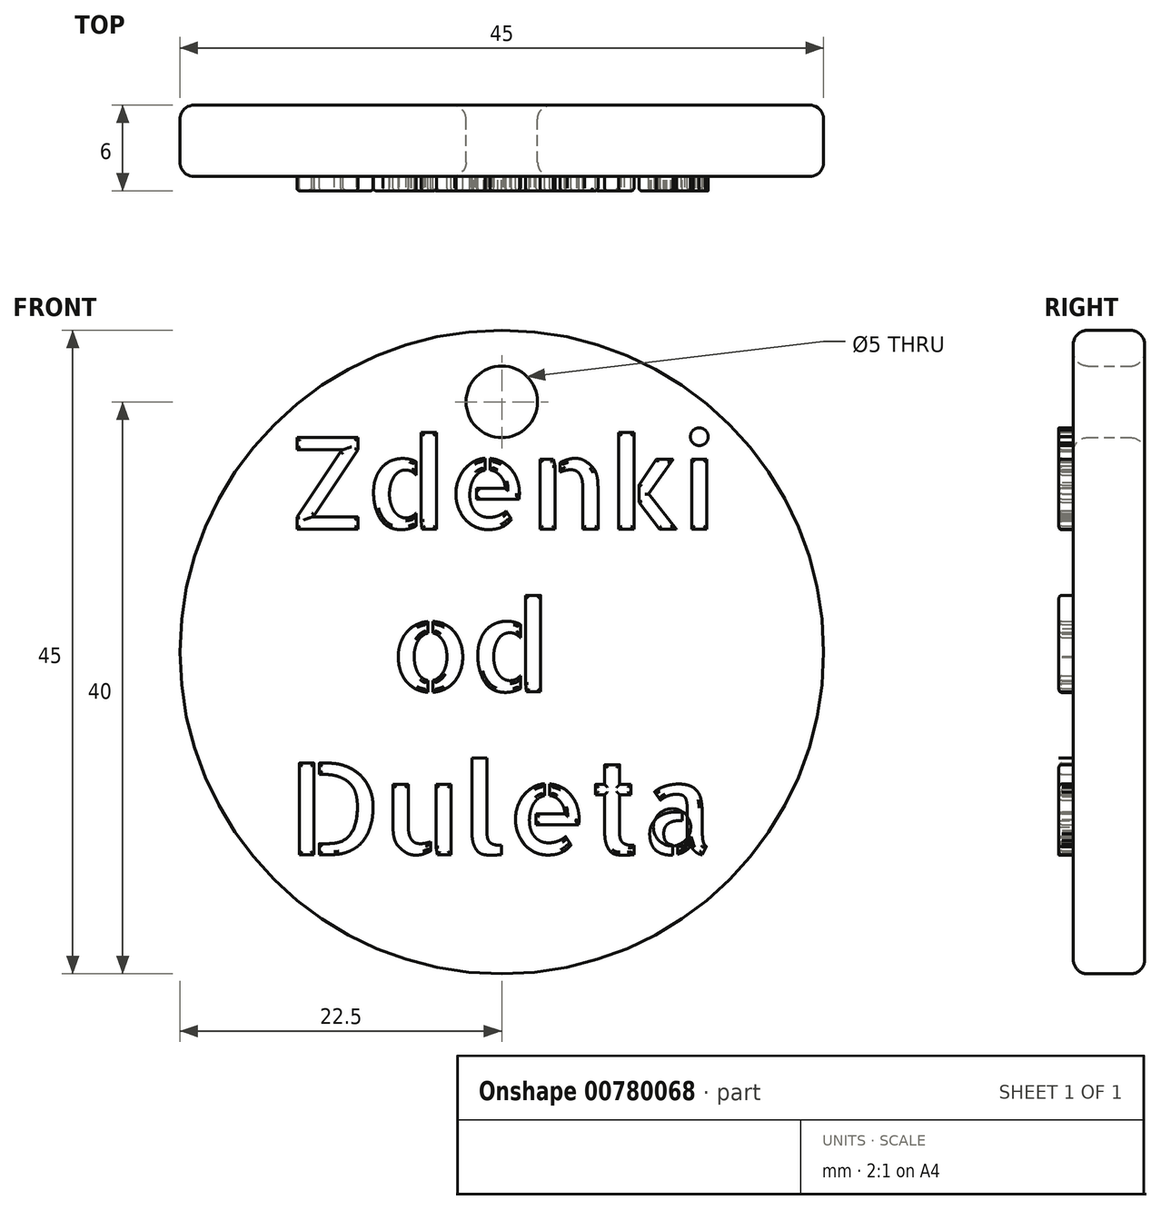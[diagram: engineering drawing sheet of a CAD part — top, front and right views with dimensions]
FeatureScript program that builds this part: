
annotation { "Feature Type Name" : "Feature", "Feature Type Description" : "" }
export const myFeature = defineFeature(function(context is Context, id is Id, definition is map)
    precondition{}
    {
        {
            var Q0;
            Q0=qCreatedBy(makeId("Front.planeOp"),FACE);
            var sketch = newSketch(context, id + "F0", { "sketchPlane" : qUnion([Q0])});
            skText(sketch, "E0", { "text": "Zdenki\n   od\nDuleta", "fontName": "AllertaStencil-Regular.ttf"});
            skCircle(sketch, "E1", {"center": v(0, 0) * mm, "radius": 22.5 * mm});
            skCircle(sketch, "E2", {"center": v(0, 17.5) * mm, "radius": 2.5 * mm});
            const initialGuessF0  = {"E0": [-0.015, 0.0086, 1, 0, 0.0064]};
            skSetInitialGuess(sketch, initialGuessF0);
            skSolve(sketch);
        }
        {
            var Q0;
            Q0=makeQuery(id+"F0.imprint","IMPRINT",FACE,{"disambiguationData":[TD([[makeQuery(id+"F0.imprint","IMPRINT",EDGE,{"derivedFrom":sQuery(id+"F0.wireOp",EDGE,"E0.sketch_text.stroke-0")}),1.0]])]});
            extrude(context, id + "F1", {"entities" : qUnion([Q0]), "depth" : 5 * mm, "offsetDistance" : 25 * mm});
        }
        {
            var Q0;
            Q0=makeQuery(id+"F0.imprint","IMPRINT",FACE,{"disambiguationData":[TD([[makeQuery(id+"F0.imprint","IMPRINT",EDGE,{"derivedFrom":sQuery(id+"F0.wireOp",EDGE,"E0.sketch_text.stroke-0")}),-1.0]])]});
            var Q1;
            Q1=makeQuery(id+"F0.imprint","IMPRINT",FACE,{"disambiguationData":[TD([[makeQuery(id+"F0.imprint","IMPRINT",EDGE,{"derivedFrom":sQuery(id+"F0.wireOp",EDGE,"E0.sketch_text.stroke-17")}),-1.0]])]});
            var Q2;
            Q2=makeQuery(id+"F0.imprint","IMPRINT",FACE,{"disambiguationData":[TD([[makeQuery(id+"F0.imprint","IMPRINT",EDGE,{"derivedFrom":sQuery(id+"F0.wireOp",EDGE,"E0.sketch_text.stroke-12")}),-1.0]])]});
            var Q3;
            Q3=makeQuery(id+"F0.imprint","IMPRINT",FACE,{"disambiguationData":[TD([[makeQuery(id+"F0.imprint","IMPRINT",EDGE,{"derivedFrom":sQuery(id+"F0.wireOp",EDGE,"E0.sketch_text.stroke-55")}),-1.0]])]});
            var Q4;
            Q4=makeQuery(id+"F0.imprint","IMPRINT",FACE,{"disambiguationData":[TD([[makeQuery(id+"F0.imprint","IMPRINT",EDGE,{"derivedFrom":sQuery(id+"F0.wireOp",EDGE,"E0.sketch_text.stroke-42")}),-1.0]])]});
            var Q5;
            Q5=makeQuery(id+"F0.imprint","IMPRINT",FACE,{"disambiguationData":[TD([[makeQuery(id+"F0.imprint","IMPRINT",EDGE,{"derivedFrom":sQuery(id+"F0.wireOp",EDGE,"E0.sketch_text.stroke-79")}),-1.0]])]});
            var Q6;
            Q6=makeQuery(id+"F0.imprint","IMPRINT",FACE,{"disambiguationData":[TD([[makeQuery(id+"F0.imprint","IMPRINT",EDGE,{"derivedFrom":sQuery(id+"F0.wireOp",EDGE,"E0.sketch_text.stroke-84")}),-1.0]])]});
            var Q7;
            Q7=makeQuery(id+"F0.imprint","IMPRINT",FACE,{"disambiguationData":[TD([[makeQuery(id+"F0.imprint","IMPRINT",EDGE,{"derivedFrom":sQuery(id+"F0.wireOp",EDGE,"E0.sketch_text.stroke-110")}),-1.0]])]});
            var Q8;
            Q8=makeQuery(id+"F0.imprint","IMPRINT",FACE,{"disambiguationData":[TD([[makeQuery(id+"F0.imprint","IMPRINT",EDGE,{"derivedFrom":sQuery(id+"F0.wireOp",EDGE,"E0.sketch_text.stroke-103")}),-1.0]])]});
            var Q9;
            Q9=makeQuery(id+"F0.imprint","IMPRINT",FACE,{"disambiguationData":[TD([[makeQuery(id+"F0.imprint","IMPRINT",EDGE,{"derivedFrom":sQuery(id+"F0.wireOp",EDGE,"E0.sketch_text.stroke-114")}),-1.0]])]});
            var Q10;
            Q10=makeQuery(id+"F0.imprint","IMPRINT",FACE,{"disambiguationData":[TD([[makeQuery(id+"F0.imprint","IMPRINT",EDGE,{"derivedFrom":sQuery(id+"F0.wireOp",EDGE,"E0.sketch_text.stroke-118")}),-1.0]])]});
            var Q11;
            Q11=makeQuery(id+"F0.imprint","IMPRINT",FACE,{"disambiguationData":[TD([[makeQuery(id+"F0.imprint","IMPRINT",EDGE,{"derivedFrom":sQuery(id+"F0.wireOp",EDGE,"E0.sketch_text.stroke-142")}),-1.0]])]});
            var Q12;
            Q12=makeQuery(id+"F0.imprint","IMPRINT",FACE,{"disambiguationData":[TD([[makeQuery(id+"F0.imprint","IMPRINT",EDGE,{"derivedFrom":sQuery(id+"F0.wireOp",EDGE,"E0.sketch_text.stroke-126")}),-1.0]])]});
            var Q13;
            Q13=makeQuery(id+"F0.imprint","IMPRINT",FACE,{"disambiguationData":[TD([[makeQuery(id+"F0.imprint","IMPRINT",EDGE,{"derivedFrom":sQuery(id+"F0.wireOp",EDGE,"E0.sketch_text.stroke-163")}),-1.0]])]});
            var Q14;
            Q14=makeQuery(id+"F0.imprint","IMPRINT",FACE,{"disambiguationData":[TD([[makeQuery(id+"F0.imprint","IMPRINT",EDGE,{"derivedFrom":sQuery(id+"F0.wireOp",EDGE,"E0.sketch_text.stroke-158")}),-1.0]])]});
            var Q15;
            Q15=makeQuery(id+"F0.imprint","IMPRINT",FACE,{"disambiguationData":[TD([[makeQuery(id+"F0.imprint","IMPRINT",EDGE,{"derivedFrom":sQuery(id+"F0.wireOp",EDGE,"E0.sketch_text.stroke-188")}),-1.0]])]});
            var Q16;
            Q16=makeQuery(id+"F0.imprint","IMPRINT",FACE,{"disambiguationData":[TD([[makeQuery(id+"F0.imprint","IMPRINT",EDGE,{"derivedFrom":sQuery(id+"F0.wireOp",EDGE,"E0.sketch_text.stroke-192")}),-1.0]])]});
            var Q17;
            Q17=makeQuery(id+"F0.imprint","IMPRINT",FACE,{"disambiguationData":[TD([[makeQuery(id+"F0.imprint","IMPRINT",EDGE,{"derivedFrom":sQuery(id+"F0.wireOp",EDGE,"E0.sketch_text.stroke-214")}),-1.0]])]});
            var Q18;
            Q18=makeQuery(id+"F0.imprint","IMPRINT",FACE,{"disambiguationData":[TD([[makeQuery(id+"F0.imprint","IMPRINT",EDGE,{"derivedFrom":sQuery(id+"F0.wireOp",EDGE,"E0.sketch_text.stroke-234")}),-1.0]])]});
            var Q19;
            Q19=makeQuery(id+"F0.imprint","IMPRINT",FACE,{"disambiguationData":[TD([[makeQuery(id+"F0.imprint","IMPRINT",EDGE,{"derivedFrom":sQuery(id+"F0.wireOp",EDGE,"E0.sketch_text.stroke-239")}),-1.0]])]});
            var Q20;
            Q20=makeQuery(id+"F0.imprint","IMPRINT",FACE,{"disambiguationData":[TD([[makeQuery(id+"F0.imprint","IMPRINT",EDGE,{"derivedFrom":sQuery(id+"F0.wireOp",EDGE,"E0.sketch_text.stroke-270")}),-1.0]])]});
            var Q21;
            Q21=makeQuery(id+"F0.imprint","IMPRINT",FACE,{"disambiguationData":[TD([[makeQuery(id+"F0.imprint","IMPRINT",EDGE,{"derivedFrom":sQuery(id+"F0.wireOp",EDGE,"E0.sketch_text.stroke-257")}),-1.0]])]});
            var Q22;
            Q22=makeQuery(id+"F0.imprint","IMPRINT",FACE,{"disambiguationData":[TD([[makeQuery(id+"F0.imprint","IMPRINT",EDGE,{"derivedFrom":sQuery(id+"F0.wireOp",EDGE,"E0.sketch_text.stroke-294")}),-1.0]])]});
            var Q23;
            Q23=makeQuery(id+"F0.imprint","IMPRINT",FACE,{"disambiguationData":[TD([[makeQuery(id+"F0.imprint","IMPRINT",EDGE,{"derivedFrom":sQuery(id+"F0.wireOp",EDGE,"E0.sketch_text.stroke-319")}),-1.0]])]});
            var Q24;
            Q24=makeQuery(id+"F0.imprint","IMPRINT",FACE,{"disambiguationData":[TD([[makeQuery(id+"F0.imprint","IMPRINT",EDGE,{"derivedFrom":sQuery(id+"F0.wireOp",EDGE,"E0.sketch_text.stroke-338")}),-1.0]])]});
            extrude(context, id + "F2", {"entities" : qUnion([Q0, Q1, Q2, Q3, Q4, Q5, Q6, Q7, Q8, Q9, Q10, Q11, Q12, Q13, Q14, Q15, Q16, Q17, Q18, Q19, Q20, Q21, Q22, Q23, Q24]), "operationType" : NewBodyOperationType.ADD, "depth" : 6 * mm, "offsetDistance" : 25 * mm});
        }
        {
            var Q0;
            Q0=makeQuery(id+"F0.imprint","IMPRINT",FACE,{"disambiguationData":[TD([[makeQuery(id+"F0.imprint","IMPRINT",EDGE,{"derivedFrom":sQuery(id+"F0.wireOp",EDGE,"E2")}),1.0]])]});
            extrude(context, id + "F3", {"entities" : qUnion([Q0]), "operationType" : NewBodyOperationType.REMOVE, "endBound" : BoundingType.THROUGH_ALL, "depth" : 25 * mm, "offsetDistance" : 25 * mm});
        }
        {
            var Q0;
            Q0=makeQuery(id+"F1.opExtrude","SWEPT_FACE",FACE,{"disambiguationData":[OSD([sQuery(id+"F0.wireOp",EDGE,"E2")])]});
            var Q1;
            Q1=makeQuery(id+"F1.opExtrude","SWEPT_FACE",FACE,{"disambiguationData":[OSD([sQuery(id+"F0.wireOp",EDGE,"E1")])]});
            fillet(context, id + "F4", {"entities" : qUnion([Q0, Q1]), "radius" : 1 * mm, "tangentPropagation" : true, "allowEdgeOverflow" : false});
        }
        {
            var Q0;
            Q0=makeQuery(id+"F2.opExtrude","CAP_FACE",FACE,{"disambiguationData":[OSD([sQuery(id+"F0.wireOp",EDGE,"E0.sketch_text.stroke-0"),sQuery(id+"F0.wireOp",EDGE,"E0.sketch_text.stroke-1"),sQuery(id+"F0.wireOp",EDGE,"E0.sketch_text.stroke-2"),sQuery(id+"F0.wireOp",EDGE,"E0.sketch_text.stroke-3"),sQuery(id+"F0.wireOp",EDGE,"E0.sketch_text.stroke-4"),sQuery(id+"F0.wireOp",EDGE,"E0.sketch_text.stroke-5"),sQuery(id+"F0.wireOp",EDGE,"E0.sketch_text.stroke-6"),sQuery(id+"F0.wireOp",EDGE,"E0.sketch_text.stroke-7"),sQuery(id+"F0.wireOp",EDGE,"E0.sketch_text.stroke-8"),sQuery(id+"F0.wireOp",EDGE,"E0.sketch_text.stroke-9"),sQuery(id+"F0.wireOp",EDGE,"E0.sketch_text.stroke-10"),sQuery(id+"F0.wireOp",EDGE,"E0.sketch_text.stroke-11")])],"isStart":false});
            var Q1;
            Q1=makeQuery(id+"F2.opExtrude","CAP_FACE",FACE,{"disambiguationData":[OSD([sQuery(id+"F0.wireOp",EDGE,"E0.sketch_text.stroke-17"),sQuery(id+"F0.wireOp",EDGE,"E0.sketch_text.stroke-18"),sQuery(id+"F0.wireOp",EDGE,"E0.sketch_text.stroke-19"),sQuery(id+"F0.wireOp",EDGE,"E0.sketch_text.stroke-20"),sQuery(id+"F0.wireOp",EDGE,"E0.sketch_text.stroke-21"),sQuery(id+"F0.wireOp",EDGE,"E0.sketch_text.stroke-22"),sQuery(id+"F0.wireOp",EDGE,"E0.sketch_text.stroke-23"),sQuery(id+"F0.wireOp",EDGE,"E0.sketch_text.stroke-24"),sQuery(id+"F0.wireOp",EDGE,"E0.sketch_text.stroke-25"),sQuery(id+"F0.wireOp",EDGE,"E0.sketch_text.stroke-26"),sQuery(id+"F0.wireOp",EDGE,"E0.sketch_text.stroke-27"),sQuery(id+"F0.wireOp",EDGE,"E0.sketch_text.stroke-28"),sQuery(id+"F0.wireOp",EDGE,"E0.sketch_text.stroke-29"),sQuery(id+"F0.wireOp",EDGE,"E0.sketch_text.stroke-30"),sQuery(id+"F0.wireOp",EDGE,"E0.sketch_text.stroke-31"),sQuery(id+"F0.wireOp",EDGE,"E0.sketch_text.stroke-32"),sQuery(id+"F0.wireOp",EDGE,"E0.sketch_text.stroke-33"),sQuery(id+"F0.wireOp",EDGE,"E0.sketch_text.stroke-34"),sQuery(id+"F0.wireOp",EDGE,"E0.sketch_text.stroke-35"),sQuery(id+"F0.wireOp",EDGE,"E0.sketch_text.stroke-36"),sQuery(id+"F0.wireOp",EDGE,"E0.sketch_text.stroke-37"),sQuery(id+"F0.wireOp",EDGE,"E0.sketch_text.stroke-38"),sQuery(id+"F0.wireOp",EDGE,"E0.sketch_text.stroke-39"),sQuery(id+"F0.wireOp",EDGE,"E0.sketch_text.stroke-40"),sQuery(id+"F0.wireOp",EDGE,"E0.sketch_text.stroke-41")])],"isStart":false});
            var Q2;
            Q2=makeQuery(id+"F2.opExtrude","CAP_FACE",FACE,{"disambiguationData":[OSD([sQuery(id+"F0.wireOp",EDGE,"E0.sketch_text.stroke-12"),sQuery(id+"F0.wireOp",EDGE,"E0.sketch_text.stroke-13"),sQuery(id+"F0.wireOp",EDGE,"E0.sketch_text.stroke-14"),sQuery(id+"F0.wireOp",EDGE,"E0.sketch_text.stroke-15"),sQuery(id+"F0.wireOp",EDGE,"E0.sketch_text.stroke-16")])],"isStart":false});
            var Q3;
            Q3=makeQuery(id+"F2.opExtrude","CAP_FACE",FACE,{"disambiguationData":[OSD([sQuery(id+"F0.wireOp",EDGE,"E0.sketch_text.stroke-55"),sQuery(id+"F0.wireOp",EDGE,"E0.sketch_text.stroke-56"),sQuery(id+"F0.wireOp",EDGE,"E0.sketch_text.stroke-57"),sQuery(id+"F0.wireOp",EDGE,"E0.sketch_text.stroke-58"),sQuery(id+"F0.wireOp",EDGE,"E0.sketch_text.stroke-59"),sQuery(id+"F0.wireOp",EDGE,"E0.sketch_text.stroke-60"),sQuery(id+"F0.wireOp",EDGE,"E0.sketch_text.stroke-61"),sQuery(id+"F0.wireOp",EDGE,"E0.sketch_text.stroke-62"),sQuery(id+"F0.wireOp",EDGE,"E0.sketch_text.stroke-63"),sQuery(id+"F0.wireOp",EDGE,"E0.sketch_text.stroke-64"),sQuery(id+"F0.wireOp",EDGE,"E0.sketch_text.stroke-65"),sQuery(id+"F0.wireOp",EDGE,"E0.sketch_text.stroke-66"),sQuery(id+"F0.wireOp",EDGE,"E0.sketch_text.stroke-67"),sQuery(id+"F0.wireOp",EDGE,"E0.sketch_text.stroke-68"),sQuery(id+"F0.wireOp",EDGE,"E0.sketch_text.stroke-69"),sQuery(id+"F0.wireOp",EDGE,"E0.sketch_text.stroke-70"),sQuery(id+"F0.wireOp",EDGE,"E0.sketch_text.stroke-71"),sQuery(id+"F0.wireOp",EDGE,"E0.sketch_text.stroke-72"),sQuery(id+"F0.wireOp",EDGE,"E0.sketch_text.stroke-73"),sQuery(id+"F0.wireOp",EDGE,"E0.sketch_text.stroke-74"),sQuery(id+"F0.wireOp",EDGE,"E0.sketch_text.stroke-75"),sQuery(id+"F0.wireOp",EDGE,"E0.sketch_text.stroke-76"),sQuery(id+"F0.wireOp",EDGE,"E0.sketch_text.stroke-77"),sQuery(id+"F0.wireOp",EDGE,"E0.sketch_text.stroke-78")])],"isStart":false});
            var Q4;
            Q4=makeQuery(id+"F2.opExtrude","CAP_FACE",FACE,{"disambiguationData":[OSD([sQuery(id+"F0.wireOp",EDGE,"E0.sketch_text.stroke-42"),sQuery(id+"F0.wireOp",EDGE,"E0.sketch_text.stroke-43"),sQuery(id+"F0.wireOp",EDGE,"E0.sketch_text.stroke-44"),sQuery(id+"F0.wireOp",EDGE,"E0.sketch_text.stroke-45"),sQuery(id+"F0.wireOp",EDGE,"E0.sketch_text.stroke-46"),sQuery(id+"F0.wireOp",EDGE,"E0.sketch_text.stroke-47"),sQuery(id+"F0.wireOp",EDGE,"E0.sketch_text.stroke-48"),sQuery(id+"F0.wireOp",EDGE,"E0.sketch_text.stroke-49"),sQuery(id+"F0.wireOp",EDGE,"E0.sketch_text.stroke-50"),sQuery(id+"F0.wireOp",EDGE,"E0.sketch_text.stroke-51"),sQuery(id+"F0.wireOp",EDGE,"E0.sketch_text.stroke-52"),sQuery(id+"F0.wireOp",EDGE,"E0.sketch_text.stroke-53"),sQuery(id+"F0.wireOp",EDGE,"E0.sketch_text.stroke-54")])],"isStart":false});
            var Q5;
            Q5=makeQuery(id+"F2.opExtrude","CAP_FACE",FACE,{"disambiguationData":[OSD([sQuery(id+"F0.wireOp",EDGE,"E0.sketch_text.stroke-79"),sQuery(id+"F0.wireOp",EDGE,"E0.sketch_text.stroke-80"),sQuery(id+"F0.wireOp",EDGE,"E0.sketch_text.stroke-81"),sQuery(id+"F0.wireOp",EDGE,"E0.sketch_text.stroke-82"),sQuery(id+"F0.wireOp",EDGE,"E0.sketch_text.stroke-83")])],"isStart":false});
            var Q6;
            Q6=makeQuery(id+"F2.opExtrude","CAP_FACE",FACE,{"disambiguationData":[OSD([sQuery(id+"F0.wireOp",EDGE,"E0.sketch_text.stroke-84"),sQuery(id+"F0.wireOp",EDGE,"E0.sketch_text.stroke-85"),sQuery(id+"F0.wireOp",EDGE,"E0.sketch_text.stroke-86"),sQuery(id+"F0.wireOp",EDGE,"E0.sketch_text.stroke-87"),sQuery(id+"F0.wireOp",EDGE,"E0.sketch_text.stroke-88"),sQuery(id+"F0.wireOp",EDGE,"E0.sketch_text.stroke-89"),sQuery(id+"F0.wireOp",EDGE,"E0.sketch_text.stroke-90"),sQuery(id+"F0.wireOp",EDGE,"E0.sketch_text.stroke-91"),sQuery(id+"F0.wireOp",EDGE,"E0.sketch_text.stroke-92"),sQuery(id+"F0.wireOp",EDGE,"E0.sketch_text.stroke-93"),sQuery(id+"F0.wireOp",EDGE,"E0.sketch_text.stroke-94"),sQuery(id+"F0.wireOp",EDGE,"E0.sketch_text.stroke-95"),sQuery(id+"F0.wireOp",EDGE,"E0.sketch_text.stroke-96"),sQuery(id+"F0.wireOp",EDGE,"E0.sketch_text.stroke-97"),sQuery(id+"F0.wireOp",EDGE,"E0.sketch_text.stroke-98"),sQuery(id+"F0.wireOp",EDGE,"E0.sketch_text.stroke-99"),sQuery(id+"F0.wireOp",EDGE,"E0.sketch_text.stroke-100"),sQuery(id+"F0.wireOp",EDGE,"E0.sketch_text.stroke-101"),sQuery(id+"F0.wireOp",EDGE,"E0.sketch_text.stroke-102")])],"isStart":false});
            var Q7;
            Q7=makeQuery(id+"F2.opExtrude","CAP_FACE",FACE,{"disambiguationData":[OSD([sQuery(id+"F0.wireOp",EDGE,"E0.sketch_text.stroke-110"),sQuery(id+"F0.wireOp",EDGE,"E0.sketch_text.stroke-111"),sQuery(id+"F0.wireOp",EDGE,"E0.sketch_text.stroke-112"),sQuery(id+"F0.wireOp",EDGE,"E0.sketch_text.stroke-113")])],"isStart":false});
            var Q8;
            Q8=makeQuery(id+"F2.opExtrude","CAP_FACE",FACE,{"disambiguationData":[OSD([sQuery(id+"F0.wireOp",EDGE,"E0.sketch_text.stroke-103"),sQuery(id+"F0.wireOp",EDGE,"E0.sketch_text.stroke-104"),sQuery(id+"F0.wireOp",EDGE,"E0.sketch_text.stroke-105"),sQuery(id+"F0.wireOp",EDGE,"E0.sketch_text.stroke-106"),sQuery(id+"F0.wireOp",EDGE,"E0.sketch_text.stroke-107"),sQuery(id+"F0.wireOp",EDGE,"E0.sketch_text.stroke-108"),sQuery(id+"F0.wireOp",EDGE,"E0.sketch_text.stroke-109")])],"isStart":false});
            var Q9;
            Q9=makeQuery(id+"F2.opExtrude","CAP_FACE",FACE,{"disambiguationData":[OSD([sQuery(id+"F0.wireOp",EDGE,"E0.sketch_text.stroke-114"),sQuery(id+"F0.wireOp",EDGE,"E0.sketch_text.stroke-115"),sQuery(id+"F0.wireOp",EDGE,"E0.sketch_text.stroke-116"),sQuery(id+"F0.wireOp",EDGE,"E0.sketch_text.stroke-117")])],"isStart":false});
            var Q10;
            Q10=makeQuery(id+"F2.opExtrude","CAP_FACE",FACE,{"disambiguationData":[OSD([sQuery(id+"F0.wireOp",EDGE,"E0.sketch_text.stroke-158"),sQuery(id+"F0.wireOp",EDGE,"E0.sketch_text.stroke-159"),sQuery(id+"F0.wireOp",EDGE,"E0.sketch_text.stroke-160"),sQuery(id+"F0.wireOp",EDGE,"E0.sketch_text.stroke-161"),sQuery(id+"F0.wireOp",EDGE,"E0.sketch_text.stroke-162")])],"isStart":false});
            var Q11;
            Q11=makeQuery(id+"F2.opExtrude","CAP_FACE",FACE,{"disambiguationData":[OSD([sQuery(id+"F0.wireOp",EDGE,"E0.sketch_text.stroke-163"),sQuery(id+"F0.wireOp",EDGE,"E0.sketch_text.stroke-164"),sQuery(id+"F0.wireOp",EDGE,"E0.sketch_text.stroke-165"),sQuery(id+"F0.wireOp",EDGE,"E0.sketch_text.stroke-166"),sQuery(id+"F0.wireOp",EDGE,"E0.sketch_text.stroke-167"),sQuery(id+"F0.wireOp",EDGE,"E0.sketch_text.stroke-168"),sQuery(id+"F0.wireOp",EDGE,"E0.sketch_text.stroke-169"),sQuery(id+"F0.wireOp",EDGE,"E0.sketch_text.stroke-170"),sQuery(id+"F0.wireOp",EDGE,"E0.sketch_text.stroke-171"),sQuery(id+"F0.wireOp",EDGE,"E0.sketch_text.stroke-172"),sQuery(id+"F0.wireOp",EDGE,"E0.sketch_text.stroke-173"),sQuery(id+"F0.wireOp",EDGE,"E0.sketch_text.stroke-174"),sQuery(id+"F0.wireOp",EDGE,"E0.sketch_text.stroke-175"),sQuery(id+"F0.wireOp",EDGE,"E0.sketch_text.stroke-176"),sQuery(id+"F0.wireOp",EDGE,"E0.sketch_text.stroke-177"),sQuery(id+"F0.wireOp",EDGE,"E0.sketch_text.stroke-178"),sQuery(id+"F0.wireOp",EDGE,"E0.sketch_text.stroke-179"),sQuery(id+"F0.wireOp",EDGE,"E0.sketch_text.stroke-180"),sQuery(id+"F0.wireOp",EDGE,"E0.sketch_text.stroke-181"),sQuery(id+"F0.wireOp",EDGE,"E0.sketch_text.stroke-182"),sQuery(id+"F0.wireOp",EDGE,"E0.sketch_text.stroke-183"),sQuery(id+"F0.wireOp",EDGE,"E0.sketch_text.stroke-184"),sQuery(id+"F0.wireOp",EDGE,"E0.sketch_text.stroke-185"),sQuery(id+"F0.wireOp",EDGE,"E0.sketch_text.stroke-186"),sQuery(id+"F0.wireOp",EDGE,"E0.sketch_text.stroke-187")])],"isStart":false});
            var Q12;
            Q12=makeQuery(id+"F2.opExtrude","CAP_FACE",FACE,{"disambiguationData":[OSD([sQuery(id+"F0.wireOp",EDGE,"E0.sketch_text.stroke-126"),sQuery(id+"F0.wireOp",EDGE,"E0.sketch_text.stroke-127"),sQuery(id+"F0.wireOp",EDGE,"E0.sketch_text.stroke-128"),sQuery(id+"F0.wireOp",EDGE,"E0.sketch_text.stroke-129"),sQuery(id+"F0.wireOp",EDGE,"E0.sketch_text.stroke-130"),sQuery(id+"F0.wireOp",EDGE,"E0.sketch_text.stroke-131"),sQuery(id+"F0.wireOp",EDGE,"E0.sketch_text.stroke-132"),sQuery(id+"F0.wireOp",EDGE,"E0.sketch_text.stroke-133"),sQuery(id+"F0.wireOp",EDGE,"E0.sketch_text.stroke-134"),sQuery(id+"F0.wireOp",EDGE,"E0.sketch_text.stroke-135"),sQuery(id+"F0.wireOp",EDGE,"E0.sketch_text.stroke-136"),sQuery(id+"F0.wireOp",EDGE,"E0.sketch_text.stroke-137"),sQuery(id+"F0.wireOp",EDGE,"E0.sketch_text.stroke-138"),sQuery(id+"F0.wireOp",EDGE,"E0.sketch_text.stroke-139"),sQuery(id+"F0.wireOp",EDGE,"E0.sketch_text.stroke-140"),sQuery(id+"F0.wireOp",EDGE,"E0.sketch_text.stroke-141")])],"isStart":false});
            var Q13;
            Q13=makeQuery(id+"F2.opExtrude","CAP_FACE",FACE,{"disambiguationData":[OSD([sQuery(id+"F0.wireOp",EDGE,"E0.sketch_text.stroke-142"),sQuery(id+"F0.wireOp",EDGE,"E0.sketch_text.stroke-143"),sQuery(id+"F0.wireOp",EDGE,"E0.sketch_text.stroke-144"),sQuery(id+"F0.wireOp",EDGE,"E0.sketch_text.stroke-145"),sQuery(id+"F0.wireOp",EDGE,"E0.sketch_text.stroke-146"),sQuery(id+"F0.wireOp",EDGE,"E0.sketch_text.stroke-147"),sQuery(id+"F0.wireOp",EDGE,"E0.sketch_text.stroke-148"),sQuery(id+"F0.wireOp",EDGE,"E0.sketch_text.stroke-149"),sQuery(id+"F0.wireOp",EDGE,"E0.sketch_text.stroke-150"),sQuery(id+"F0.wireOp",EDGE,"E0.sketch_text.stroke-151"),sQuery(id+"F0.wireOp",EDGE,"E0.sketch_text.stroke-152"),sQuery(id+"F0.wireOp",EDGE,"E0.sketch_text.stroke-153"),sQuery(id+"F0.wireOp",EDGE,"E0.sketch_text.stroke-154"),sQuery(id+"F0.wireOp",EDGE,"E0.sketch_text.stroke-155"),sQuery(id+"F0.wireOp",EDGE,"E0.sketch_text.stroke-156"),sQuery(id+"F0.wireOp",EDGE,"E0.sketch_text.stroke-157")])],"isStart":false});
            var Q14;
            Q14=makeQuery(id+"F2.opExtrude","CAP_FACE",FACE,{"disambiguationData":[OSD([sQuery(id+"F0.wireOp",EDGE,"E0.sketch_text.stroke-188"),sQuery(id+"F0.wireOp",EDGE,"E0.sketch_text.stroke-189"),sQuery(id+"F0.wireOp",EDGE,"E0.sketch_text.stroke-190"),sQuery(id+"F0.wireOp",EDGE,"E0.sketch_text.stroke-191")])],"isStart":false});
            var Q15;
            Q15=makeQuery(id+"F2.opExtrude","CAP_FACE",FACE,{"disambiguationData":[OSD([sQuery(id+"F0.wireOp",EDGE,"E0.sketch_text.stroke-192"),sQuery(id+"F0.wireOp",EDGE,"E0.sketch_text.stroke-193"),sQuery(id+"F0.wireOp",EDGE,"E0.sketch_text.stroke-194"),sQuery(id+"F0.wireOp",EDGE,"E0.sketch_text.stroke-195"),sQuery(id+"F0.wireOp",EDGE,"E0.sketch_text.stroke-196"),sQuery(id+"F0.wireOp",EDGE,"E0.sketch_text.stroke-197"),sQuery(id+"F0.wireOp",EDGE,"E0.sketch_text.stroke-198"),sQuery(id+"F0.wireOp",EDGE,"E0.sketch_text.stroke-199"),sQuery(id+"F0.wireOp",EDGE,"E0.sketch_text.stroke-200"),sQuery(id+"F0.wireOp",EDGE,"E0.sketch_text.stroke-201"),sQuery(id+"F0.wireOp",EDGE,"E0.sketch_text.stroke-202"),sQuery(id+"F0.wireOp",EDGE,"E0.sketch_text.stroke-203"),sQuery(id+"F0.wireOp",EDGE,"E0.sketch_text.stroke-204"),sQuery(id+"F0.wireOp",EDGE,"E0.sketch_text.stroke-205"),sQuery(id+"F0.wireOp",EDGE,"E0.sketch_text.stroke-206"),sQuery(id+"F0.wireOp",EDGE,"E0.sketch_text.stroke-207"),sQuery(id+"F0.wireOp",EDGE,"E0.sketch_text.stroke-208"),sQuery(id+"F0.wireOp",EDGE,"E0.sketch_text.stroke-209"),sQuery(id+"F0.wireOp",EDGE,"E0.sketch_text.stroke-210"),sQuery(id+"F0.wireOp",EDGE,"E0.sketch_text.stroke-211"),sQuery(id+"F0.wireOp",EDGE,"E0.sketch_text.stroke-212"),sQuery(id+"F0.wireOp",EDGE,"E0.sketch_text.stroke-213")])],"isStart":false});
            var Q16;
            Q16=makeQuery(id+"F2.opExtrude","CAP_FACE",FACE,{"disambiguationData":[OSD([sQuery(id+"F0.wireOp",EDGE,"E0.sketch_text.stroke-214"),sQuery(id+"F0.wireOp",EDGE,"E0.sketch_text.stroke-215"),sQuery(id+"F0.wireOp",EDGE,"E0.sketch_text.stroke-216"),sQuery(id+"F0.wireOp",EDGE,"E0.sketch_text.stroke-217"),sQuery(id+"F0.wireOp",EDGE,"E0.sketch_text.stroke-218"),sQuery(id+"F0.wireOp",EDGE,"E0.sketch_text.stroke-219"),sQuery(id+"F0.wireOp",EDGE,"E0.sketch_text.stroke-220"),sQuery(id+"F0.wireOp",EDGE,"E0.sketch_text.stroke-221"),sQuery(id+"F0.wireOp",EDGE,"E0.sketch_text.stroke-222"),sQuery(id+"F0.wireOp",EDGE,"E0.sketch_text.stroke-223"),sQuery(id+"F0.wireOp",EDGE,"E0.sketch_text.stroke-224"),sQuery(id+"F0.wireOp",EDGE,"E0.sketch_text.stroke-225"),sQuery(id+"F0.wireOp",EDGE,"E0.sketch_text.stroke-226"),sQuery(id+"F0.wireOp",EDGE,"E0.sketch_text.stroke-227"),sQuery(id+"F0.wireOp",EDGE,"E0.sketch_text.stroke-228"),sQuery(id+"F0.wireOp",EDGE,"E0.sketch_text.stroke-229"),sQuery(id+"F0.wireOp",EDGE,"E0.sketch_text.stroke-230"),sQuery(id+"F0.wireOp",EDGE,"E0.sketch_text.stroke-231"),sQuery(id+"F0.wireOp",EDGE,"E0.sketch_text.stroke-232"),sQuery(id+"F0.wireOp",EDGE,"E0.sketch_text.stroke-233")])],"isStart":false});
            var Q17;
            Q17=makeQuery(id+"F2.opExtrude","CAP_FACE",FACE,{"disambiguationData":[OSD([sQuery(id+"F0.wireOp",EDGE,"E0.sketch_text.stroke-234"),sQuery(id+"F0.wireOp",EDGE,"E0.sketch_text.stroke-235"),sQuery(id+"F0.wireOp",EDGE,"E0.sketch_text.stroke-236"),sQuery(id+"F0.wireOp",EDGE,"E0.sketch_text.stroke-237"),sQuery(id+"F0.wireOp",EDGE,"E0.sketch_text.stroke-238")])],"isStart":false});
            var Q18;
            Q18=makeQuery(id+"F2.opExtrude","CAP_FACE",FACE,{"disambiguationData":[OSD([sQuery(id+"F0.wireOp",EDGE,"E0.sketch_text.stroke-270"),sQuery(id+"F0.wireOp",EDGE,"E0.sketch_text.stroke-271"),sQuery(id+"F0.wireOp",EDGE,"E0.sketch_text.stroke-272"),sQuery(id+"F0.wireOp",EDGE,"E0.sketch_text.stroke-273"),sQuery(id+"F0.wireOp",EDGE,"E0.sketch_text.stroke-274"),sQuery(id+"F0.wireOp",EDGE,"E0.sketch_text.stroke-275"),sQuery(id+"F0.wireOp",EDGE,"E0.sketch_text.stroke-276"),sQuery(id+"F0.wireOp",EDGE,"E0.sketch_text.stroke-277"),sQuery(id+"F0.wireOp",EDGE,"E0.sketch_text.stroke-278"),sQuery(id+"F0.wireOp",EDGE,"E0.sketch_text.stroke-279"),sQuery(id+"F0.wireOp",EDGE,"E0.sketch_text.stroke-280"),sQuery(id+"F0.wireOp",EDGE,"E0.sketch_text.stroke-281"),sQuery(id+"F0.wireOp",EDGE,"E0.sketch_text.stroke-282"),sQuery(id+"F0.wireOp",EDGE,"E0.sketch_text.stroke-283"),sQuery(id+"F0.wireOp",EDGE,"E0.sketch_text.stroke-284"),sQuery(id+"F0.wireOp",EDGE,"E0.sketch_text.stroke-285"),sQuery(id+"F0.wireOp",EDGE,"E0.sketch_text.stroke-286"),sQuery(id+"F0.wireOp",EDGE,"E0.sketch_text.stroke-287"),sQuery(id+"F0.wireOp",EDGE,"E0.sketch_text.stroke-288"),sQuery(id+"F0.wireOp",EDGE,"E0.sketch_text.stroke-289"),sQuery(id+"F0.wireOp",EDGE,"E0.sketch_text.stroke-290"),sQuery(id+"F0.wireOp",EDGE,"E0.sketch_text.stroke-291"),sQuery(id+"F0.wireOp",EDGE,"E0.sketch_text.stroke-292"),sQuery(id+"F0.wireOp",EDGE,"E0.sketch_text.stroke-293")])],"isStart":false});
            var Q19;
            Q19=makeQuery(id+"F2.opExtrude","CAP_FACE",FACE,{"disambiguationData":[OSD([sQuery(id+"F0.wireOp",EDGE,"E0.sketch_text.stroke-257"),sQuery(id+"F0.wireOp",EDGE,"E0.sketch_text.stroke-258"),sQuery(id+"F0.wireOp",EDGE,"E0.sketch_text.stroke-259"),sQuery(id+"F0.wireOp",EDGE,"E0.sketch_text.stroke-260"),sQuery(id+"F0.wireOp",EDGE,"E0.sketch_text.stroke-261"),sQuery(id+"F0.wireOp",EDGE,"E0.sketch_text.stroke-262"),sQuery(id+"F0.wireOp",EDGE,"E0.sketch_text.stroke-263"),sQuery(id+"F0.wireOp",EDGE,"E0.sketch_text.stroke-264"),sQuery(id+"F0.wireOp",EDGE,"E0.sketch_text.stroke-265"),sQuery(id+"F0.wireOp",EDGE,"E0.sketch_text.stroke-266"),sQuery(id+"F0.wireOp",EDGE,"E0.sketch_text.stroke-267"),sQuery(id+"F0.wireOp",EDGE,"E0.sketch_text.stroke-268"),sQuery(id+"F0.wireOp",EDGE,"E0.sketch_text.stroke-269")])],"isStart":false});
            var Q20;
            Q20=makeQuery(id+"F2.opExtrude","CAP_FACE",FACE,{"disambiguationData":[OSD([sQuery(id+"F0.wireOp",EDGE,"E0.sketch_text.stroke-294"),sQuery(id+"F0.wireOp",EDGE,"E0.sketch_text.stroke-295"),sQuery(id+"F0.wireOp",EDGE,"E0.sketch_text.stroke-296"),sQuery(id+"F0.wireOp",EDGE,"E0.sketch_text.stroke-297"),sQuery(id+"F0.wireOp",EDGE,"E0.sketch_text.stroke-298"),sQuery(id+"F0.wireOp",EDGE,"E0.sketch_text.stroke-299"),sQuery(id+"F0.wireOp",EDGE,"E0.sketch_text.stroke-300"),sQuery(id+"F0.wireOp",EDGE,"E0.sketch_text.stroke-301"),sQuery(id+"F0.wireOp",EDGE,"E0.sketch_text.stroke-302"),sQuery(id+"F0.wireOp",EDGE,"E0.sketch_text.stroke-303"),sQuery(id+"F0.wireOp",EDGE,"E0.sketch_text.stroke-304"),sQuery(id+"F0.wireOp",EDGE,"E0.sketch_text.stroke-305"),sQuery(id+"F0.wireOp",EDGE,"E0.sketch_text.stroke-306"),sQuery(id+"F0.wireOp",EDGE,"E0.sketch_text.stroke-307"),sQuery(id+"F0.wireOp",EDGE,"E0.sketch_text.stroke-308"),sQuery(id+"F0.wireOp",EDGE,"E0.sketch_text.stroke-309"),sQuery(id+"F0.wireOp",EDGE,"E0.sketch_text.stroke-310"),sQuery(id+"F0.wireOp",EDGE,"E0.sketch_text.stroke-311"),sQuery(id+"F0.wireOp",EDGE,"E0.sketch_text.stroke-312"),sQuery(id+"F0.wireOp",EDGE,"E0.sketch_text.stroke-313"),sQuery(id+"F0.wireOp",EDGE,"E0.sketch_text.stroke-314"),sQuery(id+"F0.wireOp",EDGE,"E0.sketch_text.stroke-315"),sQuery(id+"F0.wireOp",EDGE,"E0.sketch_text.stroke-316"),sQuery(id+"F0.wireOp",EDGE,"E0.sketch_text.stroke-317"),sQuery(id+"F0.wireOp",EDGE,"E0.sketch_text.stroke-318")])],"isStart":false});
            var Q21;
            Q21=makeQuery(id+"F2.opExtrude","CAP_FACE",FACE,{"disambiguationData":[OSD([sQuery(id+"F0.wireOp",EDGE,"E0.sketch_text.stroke-338"),sQuery(id+"F0.wireOp",EDGE,"E0.sketch_text.stroke-339"),sQuery(id+"F0.wireOp",EDGE,"E0.sketch_text.stroke-340"),sQuery(id+"F0.wireOp",EDGE,"E0.sketch_text.stroke-341"),sQuery(id+"F0.wireOp",EDGE,"E0.sketch_text.stroke-342"),sQuery(id+"F0.wireOp",EDGE,"E0.sketch_text.stroke-343"),sQuery(id+"F0.wireOp",EDGE,"E0.sketch_text.stroke-344"),sQuery(id+"F0.wireOp",EDGE,"E0.sketch_text.stroke-345"),sQuery(id+"F0.wireOp",EDGE,"E0.sketch_text.stroke-346"),sQuery(id+"F0.wireOp",EDGE,"E0.sketch_text.stroke-347"),sQuery(id+"F0.wireOp",EDGE,"E0.sketch_text.stroke-348"),sQuery(id+"F0.wireOp",EDGE,"E0.sketch_text.stroke-349"),sQuery(id+"F0.wireOp",EDGE,"E0.sketch_text.stroke-350"),sQuery(id+"F0.wireOp",EDGE,"E0.sketch_text.stroke-351"),sQuery(id+"F0.wireOp",EDGE,"E0.sketch_text.stroke-352"),sQuery(id+"F0.wireOp",EDGE,"E0.sketch_text.stroke-353"),sQuery(id+"F0.wireOp",EDGE,"E0.sketch_text.stroke-354"),sQuery(id+"F0.wireOp",EDGE,"E0.sketch_text.stroke-355"),sQuery(id+"F0.wireOp",EDGE,"E0.sketch_text.stroke-356"),sQuery(id+"F0.wireOp",EDGE,"E0.sketch_text.stroke-357"),sQuery(id+"F0.wireOp",EDGE,"E0.sketch_text.stroke-358"),sQuery(id+"F0.wireOp",EDGE,"E0.sketch_text.stroke-359"),sQuery(id+"F0.wireOp",EDGE,"E0.sketch_text.stroke-360"),sQuery(id+"F0.wireOp",EDGE,"E0.sketch_text.stroke-361"),sQuery(id+"F0.wireOp",EDGE,"E0.sketch_text.stroke-362"),sQuery(id+"F0.wireOp",EDGE,"E0.sketch_text.stroke-363"),sQuery(id+"F0.wireOp",EDGE,"E0.sketch_text.stroke-364"),sQuery(id+"F0.wireOp",EDGE,"E0.sketch_text.stroke-365"),sQuery(id+"F0.wireOp",EDGE,"E0.sketch_text.stroke-366"),sQuery(id+"F0.wireOp",EDGE,"E0.sketch_text.stroke-367"),sQuery(id+"F0.wireOp",EDGE,"E0.sketch_text.stroke-368"),sQuery(id+"F0.wireOp",EDGE,"E0.sketch_text.stroke-369"),sQuery(id+"F0.wireOp",EDGE,"E0.sketch_text.stroke-370"),sQuery(id+"F0.wireOp",EDGE,"E0.sketch_text.stroke-371"),sQuery(id+"F0.wireOp",EDGE,"E0.sketch_text.stroke-372"),sQuery(id+"F0.wireOp",EDGE,"E0.sketch_text.stroke-373")])],"isStart":false});
            fillet(context, id + "F5", {"entities" : qUnion([Q0, Q1, Q2, Q3, Q4, Q5, Q6, Q7, Q8, Q9, Q10, Q11, Q12, Q13, Q14, Q15, Q16, Q17, Q18, Q19, Q20, Q21]), "radius" : .2 * mm, "tangentPropagation" : true, "allowEdgeOverflow" : false});
        }
    });
